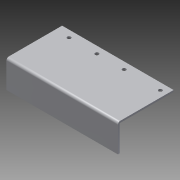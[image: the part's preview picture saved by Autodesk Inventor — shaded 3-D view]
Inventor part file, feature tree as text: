
AUTODESK INVENTOR PART (.ipt)
format: ipt  version: 2013 (Build 170138000, 138)  size: 109,568 bytes
history: native  units: in
note: dims shown in document units (in); Inventor stores cm internally (conversion verified against a paired STEP export)
features: sheet_metal_op x4, sketch x2, other x2
ambient origin geometry x8: Origin, YZ Plane, XZ Plane, XY Plane, X Axis, Y Axis, Z Axis, Center Point
bodies: Solid1 (feature_tree)
feature tree (8):
  sheet_metal_op  "Face1"
  sheet_metal_op  "Flange1"
  sketch  "Sketch1"  dims[d0=2.5984in]
  other  "Plate1"
  sketch  "Sketch2"  dims[d1=0.26in d2=0.26in d3=1.0in d4=1.75in d6=2.0in d7=2.0in d8=3.0in d9=8.0in d10=0.125in d11=0.125in d12=0.0625in d13=0.25in d14=0.125in d15=2.0in d16=90.0deg d17=0.05in d18=0.5in d19=0.125in d20=0.125in]
  other  "Plate2"
  sheet_metal_op  "Bend1"
  sheet_metal_op  "Corner1"
